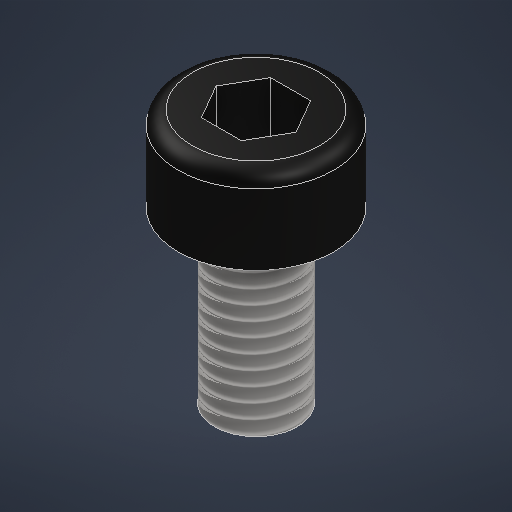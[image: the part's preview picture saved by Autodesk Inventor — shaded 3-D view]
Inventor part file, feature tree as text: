
AUTODESK INVENTOR PART (.ipt)
format: ipt  version: 2025.1 (Build 291241000, 241)  size: 267,776 bytes
history: native  units: mm
features: extrude x3, sketch x1, fillet x1, thread x1
ambient origin geometry x8: Origin, YZ Plane, XZ Plane, XY Plane, X Axis, Y Axis, Z Axis, Center Point
bodies: Solid1 (feature_tree)
feature tree (6):
  sketch  "Sketch1"  dims[d0=2.93mm d1=5.5mm d2=3.0mm d3=0.0mm d4=6.0mm d5=0.0mm d8=2.45mm d9=2.0mm d10=0.0mm d11=0.5mm d12=16.0mm d13=0.0mm]
  extrude  "Extrusion1"  Depth=0.5mm
  extrude  "Extrusion2"  Depth=3.0mm TaperAngle=0.0deg
  extrude  "Extrusion3"  Depth=6.0mm
  fillet  "Fillet1"  [1 undecoded]
  thread  "Thread2"  [1 undecoded]
note: 2 required parameter values undecoded (feature->parameter linkage not recoverable at this tier; creation-order binding heuristic only, values carry confidence <= 0.55)
